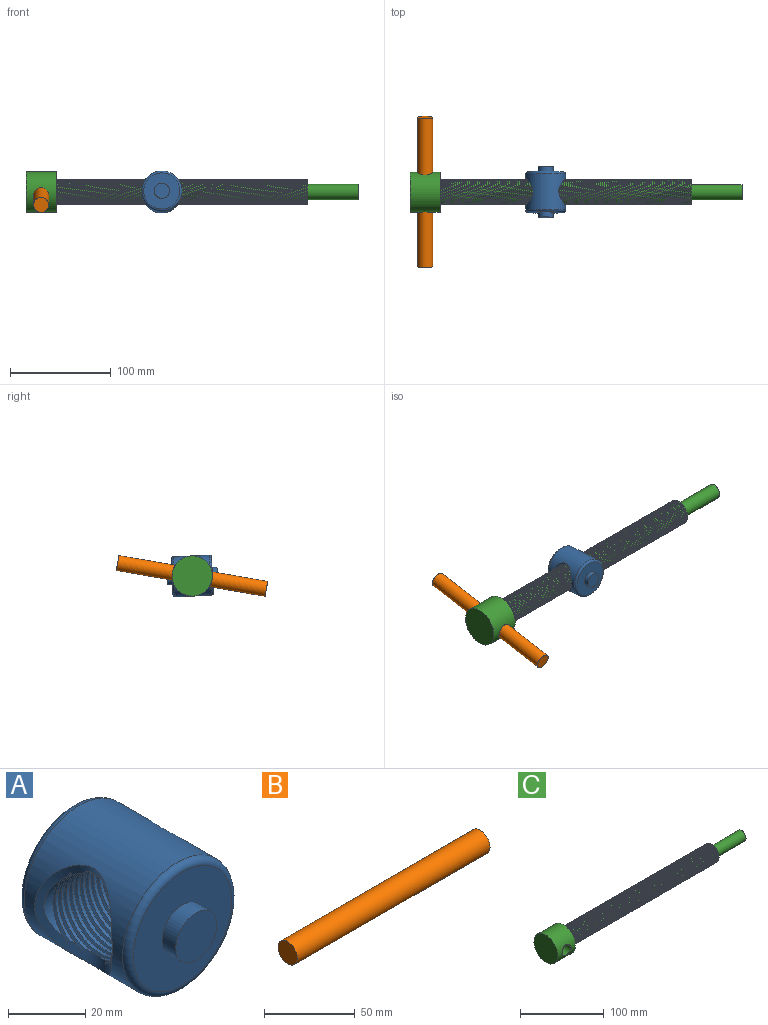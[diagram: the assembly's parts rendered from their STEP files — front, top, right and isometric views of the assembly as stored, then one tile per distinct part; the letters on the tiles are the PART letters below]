
ASSEMBLY  parts=3 mates=2
PART A: 33 faces, bbox 43.3x50x43.3 mm
  f0: bspline ~38.52x25.02mm, area 29.6mm2, adj f3,f5,f30
  f1: bspline ~38.52x33.36mm, area 1011mm2, adj f2,f4,f5,f29,f30
  f2: bspline ~30.87x27.78mm, area 1006.4mm2, adj f1,f5,f12,f29,f30
  f3: bspline ~30.87x20.05mm, area 27.5mm2, adj f0,f14,f30
  f4: bspline ~30.87x20.05mm, area 32.3mm2, adj f1,f6,f30
  f5: cylinder r=12.5mm len=26.69mm, axis (1,0,0), area 1015.8mm2, adj f0,f1,f2,f7,f29,f30
  f6: cylinder r=12.5mm len=22.77mm, axis (1,0,0), area 82.3mm2, adj f4,f8,f10,f28,f30
  f7: bspline ~30.87x20.05mm, area 29.6mm2, adj f5,f11,f29
  f8: bspline ~11.58x7.12mm, area 12.4mm2, adj f6,f10,f28,f30
  f9: bspline ~23.15x8.8mm, area 25.6mm2, adj f13,f16,f29
  f10: bspline ~14.45x10.43mm, area 13.4mm2, adj f6,f8,f28,f30
  f11: bspline ~30.87x20.05mm, area 27.5mm2, adj f7,f15,f29
  f12: bspline ~38.52x25.02mm, area 32.3mm2, adj f2,f16,f29
  f13: bspline ~28.89x10.43mm, area 23.7mm2, adj f9,f17,f29
  f14: cylinder r=12.5mm len=20.84mm, axis (1,0,0), area 0mm2, adj f3,f30
  f15: cylinder r=12.5mm len=20.84mm, axis (1,0,0), area 57.6mm2, adj f11,f25,f26,f27,f29
  f16: cylinder r=12.5mm len=22.77mm, axis (1,0,0), area 26.7mm2, adj f9,f12,f29
  f17: cylinder r=12.5mm len=18.55mm, axis (1,0,0), area 0mm2, adj f13,f29
  f18: cylinder r=20mm len=40mm, axis (0,1,0), area 3009.4mm2, adj f29,f30,f31,f32
  f19: plane 36x36mm, normal (0,-1,0), area 841.2mm2, adj f23,f31
  f20: plane 36x36mm, normal (0,1,0), area 841.2mm2, adj f22,f32
  f21: plane 15x15mm, normal (0,1,0), area 176.7mm2, adj f22
  f22: cylinder r=7.5mm len=15mm, axis (0,1,0), area 235.6mm2, adj f20,f21
  f23: cylinder r=7.5mm len=15mm, axis (0,1,0), area 235.6mm2, adj f19,f24
  f24: plane 15x15mm, normal (0,-1,0), area 176.7mm2, adj f23
  f25: bspline ~11.58x7.12mm, area 11.4mm2, adj f15,f26,f27,f29
  f26: bspline ~14.45x10.43mm, area 10.4mm2, adj f15,f25,f27,f29
  f27: plane 1x0.87mm, normal (0,0,-1), area 0.4mm2, adj f15,f25,f26
  f28: plane 1x0.87mm, normal (0,0,1), area 0.4mm2, adj f6,f8,f10
  f29: bspline ~30.95x28.33mm, area 242.4mm2, adj f1,f2,f5,f7,f9,f11,f12,f13
  f30: bspline ~30.94x28.34mm, area 244.7mm2, adj f0,f1,f2,f3,f4,f5,f6,f8
  f31: torus R=18mm, axis (0,-1,0), area 380.4mm2, adj f18,f19
  f32: torus R=18mm, axis (0,-1,0), area 380.4mm2, adj f18,f20
PART B: 3 faces, bbox 150x15x15 mm
  f0: plane 15x15mm, normal (-1,0,0), area 176.7mm2, adj f2
  f1: plane 15x15mm, normal (1,0,0), area 176.7mm2, adj f2
  f2: cylinder r=7.5mm len=150mm, axis (-1,0,0), area 7068.6mm2, adj f0,f1
PART C: 16 faces, bbox 330.3x40.3x40.3 mm
  f0: plane 15x15mm, normal (1,0,0), area 176.7mm2, adj f1
  f1: cylinder r=7.5mm len=50mm, axis (-1,0,0), area 2356.2mm2, adj f0,f2
  f2: plane 25.27x24.44mm, normal (1,0,0), area 297.2mm2, adj f1,f3,f11,f14,f15
  f3: cylinder r=12.5mm len=250mm, axis (-1,0,0), area 11961.7mm2, adj f2,f4,f9,f10,f11,f12,f15
  f4: plane 40x40mm, normal (1,0,0), area 765.8mm2, adj f3,f5,f8
  f5: cylinder r=20mm len=40mm, axis (-1,0,0), area 3409.1mm2, adj f4,f6,f7
  f6: plane 40x40mm, normal (-1,0,0), area 1256.6mm2, adj f5
  f7: cylinder r=7.5mm len=40mm, axis (0,-1,0), area 1816.8mm2, adj f5
  f8: cylinder r=12.5mm len=13.39mm, axis (-1,0,0), area 5.4mm2, adj f4,f10,f12
  f9: plane 0.63x0.39mm, normal (0,0,1), area 0mm2, adj f3,f12,f15
  f10: plane 1.3x1.12mm, normal (0,0,-1), area 0.4mm2, adj f3,f8,f11,f12,f13,f14
  f11: bspline ~250.52x28.87mm, area 7680.7mm2, adj f2,f3,f10,f14
  f12: bspline ~250.86x28.87mm, area 7721mm2, adj f3,f8,f9,f10,f13
  f13: bspline ~250.83x28.87mm, area 2459.1mm2, adj f10,f12,f14,f15
  f14: bspline ~250.5x28.87mm, area 2458.4mm2, adj f2,f10,f11,f13
  f15: bspline ~25.26x18.75mm, area 9.6mm2, adj f2,f3,f9,f13
PLACE A rot(axis=(-1,0,0),2.9deg) t=(155,19.54,3.96)mm fixed
PLACE B rot(axis=(0.61,-0.51,-0.61),125.9deg) t=(35.07,73.67,17.89)mm
PLACE C rot(axis=(-1,0,0),170.1deg) t=(20.07,-0.44,4.98)mm
MATE cylindrical A.f5 <-> C.f1  axis (1,0,0) through (138.46,-0.44,4.98)mm
MATE cylindrical B.f2 <-> C.f7  axis (0,0.99,0.17) through (35.07,-0.21,5.02)mm
